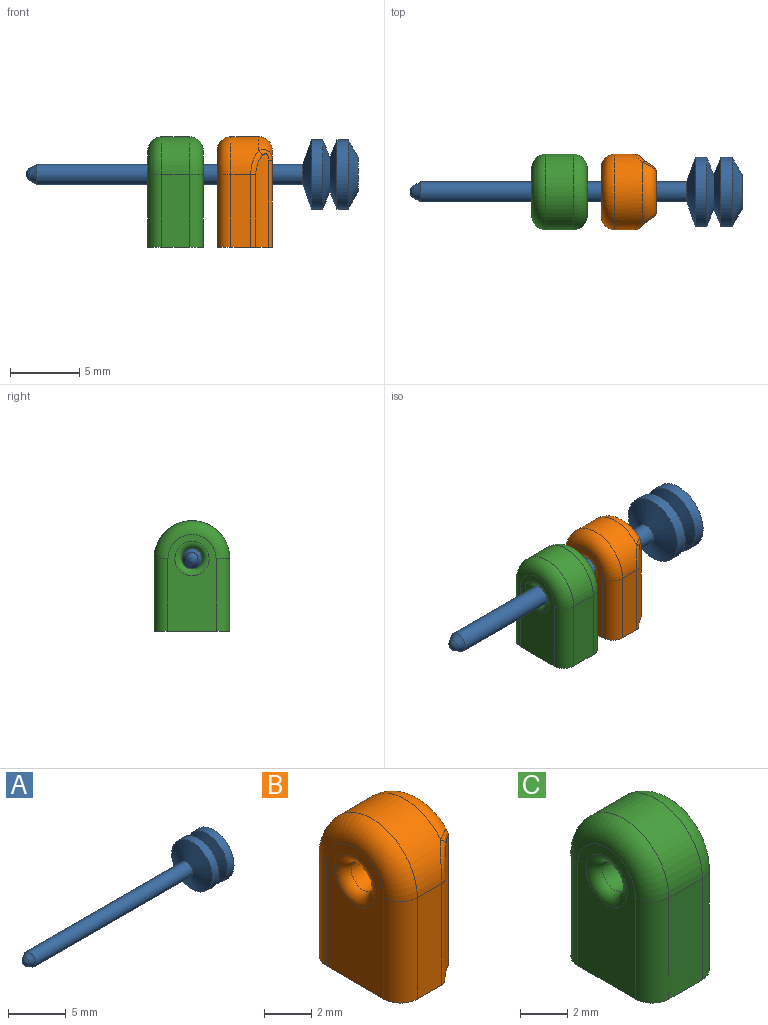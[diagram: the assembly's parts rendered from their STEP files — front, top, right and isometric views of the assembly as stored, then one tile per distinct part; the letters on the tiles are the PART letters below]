
ASSEMBLY  parts=3 mates=3
PART A: 10 faces, bbox 24x5x5 mm
  f0: plane 2.51x2.51mm, normal (1,0,0), area 5mm2, adj f1
  f1: cone r=1.26mm half-angle=60deg, axis (-1,0,0), area 17mm2, adj f0,f2
  f2: cylinder r=2.5mm len=5mm, axis (-1,0,0), area 12.6mm2, adj f1,f3
  f3: cone r=2.5mm half-angle=67.5deg, axis (1,0,0), area 15.9mm2, adj f2,f4
  f4: cone r=1.25mm half-angle=67.5deg, axis (-1,0,0), area 15.9mm2, adj f3,f5
  f5: cylinder r=2.5mm len=5mm, axis (-1,0,0), area 12.6mm2, adj f4,f6
  f6: cone r=2.5mm half-angle=70deg, axis (1,0,0), area 19.1mm2, adj f5,f7
  f7: cylinder r=0.72mm len=19.24mm, axis (-1,0,0), area 87.7mm2, adj f6,f8
  f8: cone r=0.72mm half-angle=30deg, axis (1,0,0), area 2.1mm2, adj f7,f9
  f9: sphere r=0.5mm, area 0.8mm2, adj f8
PART B: 23 faces, bbox 4.1x5.9x8.2 mm
  f0: plane 5.27x1.44mm, normal (0,-1,0), area 7.6mm2, adj f1,f5,f9,f15
  f1: plane 5.47x4mm, normal (0,0,-1), area 19.9mm2, adj f0,f2,f3,f6,f9,f11,f13,f14
  f2: plane 5.27x1.44mm, normal (0,1,0), area 7.6mm2, adj f1,f5,f11,f19
  f3: plane 7x2.84mm, normal (1,0,0), area 14.5mm2, adj f1,f8,f12,f18,f22
  f4: cylinder r=0.73mm len=3mm, axis (-1,0,0), area 13.9mm2, adj f7,f8
  f5: cylinder r=2.73mm len=5.47mm, axis (-1,0,0), area 15.8mm2, adj f0,f2,f10,f12,f16,f20
  f6: plane 7x3.47mm, normal (-1,0,0), area 18.2mm2, adj f1,f7,f9,f10,f11
  f7: torus R=1.23mm, axis (1,0,0), area 4.5mm2, adj f4,f6
  f8: torus R=1.23mm, axis (1,0,0), area 4.5mm2, adj f3,f4
  f9: cylinder r=1mm len=5.27mm, axis (0,0,-1), area 8.3mm2, adj f0,f1,f6,f10
  f10: torus R=1.74mm, axis (1,0,0), area 11.7mm2, adj f5,f6,f9,f11
  f11: cylinder r=1mm len=5.27mm, axis (0,0,1), area 8.3mm2, adj f1,f2,f6,f10
  f12: torus R=1.74mm, axis (1,0,0), area 6.3mm2, adj f3,f5,f17,f21
  f13: cylinder r=4.5mm len=6.76mm, axis (0,0,-1), area 7.8mm2, adj f1,f19,f20,f21,f22
  f14: cylinder r=4.5mm len=6.76mm, axis (0,0,-1), area 7.8mm2, adj f1,f15,f16,f17,f18
  f15: cylinder r=0.5mm len=5.27mm, axis (0,0,-1), area 2.1mm2, adj f0,f1,f14,f16
  f16: bspline ~2.54x1.25mm, area 0.7mm2, adj f5,f14,f15,f17
  f17: bspline ~1.21x1.12mm, area 0.5mm2, adj f12,f14,f16,f18
  f18: cylinder r=0.5mm len=6.26mm, axis (0,0,-1), area 3.3mm2, adj f1,f3,f14,f17
  f19: cylinder r=0.5mm len=5.27mm, axis (0,0,-1), area 2.1mm2, adj f1,f2,f13,f20
  f20: bspline ~2.2x1.25mm, area 0.7mm2, adj f5,f13,f19,f21
  f21: bspline ~1.26x1.21mm, area 0.5mm2, adj f12,f13,f20,f22
  f22: cylinder r=0.5mm len=6.26mm, axis (0,0,-1), area 3.3mm2, adj f1,f3,f13,f21
PART C: 15 faces, bbox 4x5.9x8.2 mm
  f0: plane 5.27x2mm, normal (0,-1,0), area 10.5mm2, adj f1,f4,f9,f12
  f1: plane 5.47x4mm, normal (0,0,-1), area 21mm2, adj f0,f2,f5,f6,f9,f11,f12,f14
  f2: plane 5.27x2mm, normal (0,1,0), area 10.5mm2, adj f1,f4,f11,f14
  f3: cylinder r=0.73mm len=3mm, axis (1,0,0), area 13.9mm2, adj f7,f8
  f4: cylinder r=2.73mm len=5.47mm, axis (1,0,0), area 17.2mm2, adj f0,f2,f10,f13
  f5: plane 7x3.47mm, normal (-1,0,0), area 18.2mm2, adj f1,f8,f12,f13,f14
  f6: plane 7x3.47mm, normal (1,0,0), area 18.2mm2, adj f1,f7,f9,f10,f11
  f7: torus R=1.23mm, axis (-1,0,0), area 4.5mm2, adj f3,f6
  f8: torus R=1.23mm, axis (-1,0,0), area 4.5mm2, adj f3,f5
  f9: cylinder r=1mm len=5.27mm, axis (0,0,-1), area 8.3mm2, adj f0,f1,f6,f10
  f10: torus R=1.74mm, axis (-1,0,0), area 11.7mm2, adj f4,f6,f9,f11
  f11: cylinder r=1mm len=5.27mm, axis (0,0,1), area 8.3mm2, adj f1,f2,f6,f10
  f12: cylinder r=1mm len=5.27mm, axis (0,0,1), area 8.3mm2, adj f0,f1,f5,f13
  f13: torus R=1.74mm, axis (-1,0,0), area 11.7mm2, adj f4,f5,f12,f14
  f14: cylinder r=1mm len=5.27mm, axis (0,0,-1), area 8.3mm2, adj f1,f2,f5,f13
PLACE A t=(-9.3,-0.56,5.21)mm
PLACE B t=(0,-0.56,2.58)mm fixed
PLACE C t=(-0.5,-0.56,2.58)mm
MATE slider C.f4 <-> A.f6  axis (-1,0,0) through (-5,-0.56,5.21)mm
MATE parallel C.f6 <-> B.f6  axis (1,0,0) through (-1,-0.56,2.76)mm
MATE slider A.f6 <-> B.f4  axis (-1,0,0) through (-3.43,-0.56,5.21)mm
